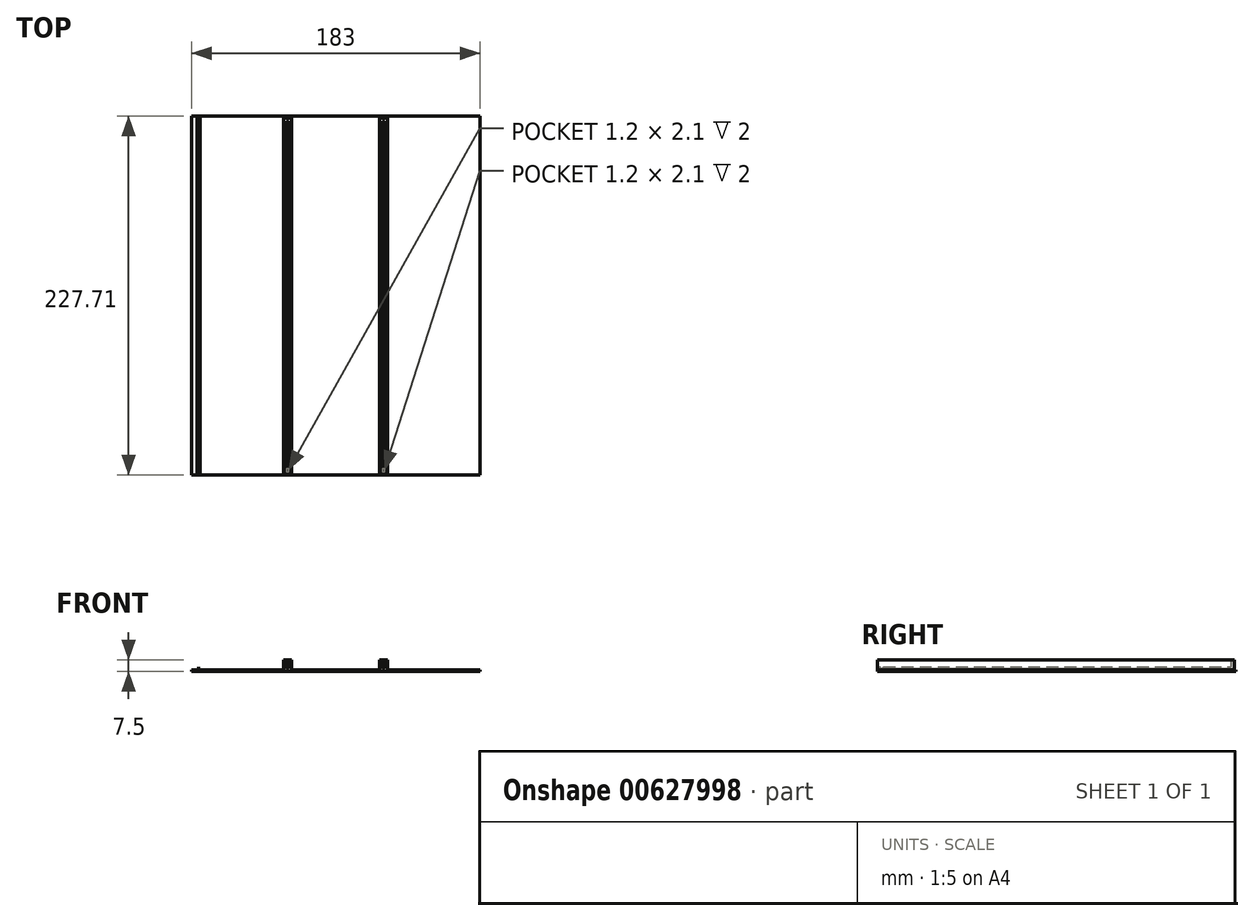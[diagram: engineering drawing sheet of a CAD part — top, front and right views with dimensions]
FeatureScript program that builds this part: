
annotation { "Feature Type Name" : "Feature", "Feature Type Description" : "" }
export const myFeature = defineFeature(function(context is Context, id is Id, definition is map)
    precondition{}
    {
        {
            var Q0;
            Q0=qCreatedBy(makeId("Top.planeOp"),FACE);
            var sketch = newSketch(context, id + "F0", { "sketchPlane" : qUnion([Q0])});
            skLineSegment(sketch, "E0.bottom", {"start": v(0, 0) * mm, "end": v(5.2, 0) * mm});
            skLineSegment(sketch, "E0.top", {"start": v(0, 226.71) * mm, "end": v(5.2, 226.71) * mm});
            skLineSegment(sketch, "E0.left", {"start": v(0, 0) * mm, "end": v(0, 226.71) * mm});
            skLineSegment(sketch, "E0.right", {"start": v(5.2, 0) * mm, "end": v(5.2, 226.71) * mm});
            skLineSegment(sketch, "E1.1.0.0", {"start": v(66.2, 0) * mm, "end": v(66.2, 226.71) * mm});
            skLineSegment(sketch, "E1.1.0.1", {"start": v(61, 0) * mm, "end": v(61, 226.71) * mm});
            skLineSegment(sketch, "E1.1.0.2", {"start": v(61, 226.71) * mm, "end": v(66.2, 226.71) * mm});
            skLineSegment(sketch, "E1.1.0.3", {"start": v(61, 0) * mm, "end": v(66.2, 0) * mm});
            skLineSegment(sketch, "E1.2.0.0", {"start": v(127.2, 0) * mm, "end": v(127.2, 226.71) * mm});
            skLineSegment(sketch, "E1.2.0.1", {"start": v(122, 0) * mm, "end": v(122, 226.71) * mm});
            skLineSegment(sketch, "E1.2.0.2", {"start": v(122, 226.71) * mm, "end": v(127.2, 226.71) * mm});
            skLineSegment(sketch, "E1.2.0.3", {"start": v(122, 0) * mm, "end": v(127.2, 0) * mm});
            skLineSegment(sketch, "E1.direction1", {"start": v(0, 0) * mm, "end": v(61, 0) * mm, "construction": true});
            skSolve(sketch);
        }
        {
            var Q0;
            Q0=makeQuery(id+"F0.imprint","IMPRINT",FACE,{"disambiguationData":[TD([[makeQuery(id+"F0.imprint","IMPRINT",EDGE,{"derivedFrom":sQuery(id+"F0.wireOp",EDGE,"E0.bottom")}),1.0]])]});
            var Q1;
            Q1=makeQuery(id+"F0.imprint","IMPRINT",FACE,{"disambiguationData":[TD([[makeQuery(id+"F0.imprint","IMPRINT",EDGE,{"derivedFrom":sQuery(id+"F0.wireOp",EDGE,"E1.1.0.0")}),1.0]])]});
            extrude(context, id + "F1", {"entities" : qUnion([Q0, Q1]), "depth" : 2 * mm, "offsetDistance" : 25 * mm});
        }
        {
            var Q0;
            Q0=makeQuery(id+"F1.opExtrude","CAP_FACE",FACE,{"disambiguationData":[OSD([sQuery(id+"F0.wireOp",EDGE,"E0.bottom"),sQuery(id+"F0.wireOp",EDGE,"E0.top"),sQuery(id+"F0.wireOp",EDGE,"E0.left"),sQuery(id+"F0.wireOp",EDGE,"E0.right")])],"isStart":false});
            var sketch = newSketch(context, id + "F2", { "sketchPlane" : qUnion([Q0])});
            skLineSegment(sketch, "E2.bottom", {"start": v(0, 0) * mm, "end": v(2, 0) * mm});
            skLineSegment(sketch, "E2.top", {"start": v(0, 226.71) * mm, "end": v(5.2, 226.71) * mm});
            skLineSegment(sketch, "E2.left", {"start": v(0, 0) * mm, "end": v(0, 226.71) * mm});
            skLineSegment(sketch, "E2.right", {"start": v(5.2, 0) * mm, "end": v(5.2, 226.71) * mm});
            skLineSegment(sketch, "E3.top", {"start": v(2, 224.71) * mm, "end": v(3.2, 224.71) * mm});
            skLineSegment(sketch, "E3.left", {"start": v(2, 0) * mm, "end": v(2, 224.71) * mm});
            skLineSegment(sketch, "E3.right", {"start": v(3.2, 0) * mm, "end": v(3.2, 224.71) * mm});
            skLineSegment(sketch, "E4.trimOffspring", {"start": v(3.2, 0) * mm, "end": v(5.2, 0) * mm});
            skLineSegment(sketch, "E5.1.0.0", {"start": v(61, 0) * mm, "end": v(61, 226.71) * mm});
            skLineSegment(sketch, "E5.1.0.1", {"start": v(66.2, 0) * mm, "end": v(66.2, 226.71) * mm});
            skLineSegment(sketch, "E5.1.0.2", {"start": v(63, 0) * mm, "end": v(63, 224.71) * mm});
            skLineSegment(sketch, "E5.1.0.3", {"start": v(64.2, 0) * mm, "end": v(64.2, 224.71) * mm});
            skLineSegment(sketch, "E5.1.0.4", {"start": v(64.2, 0) * mm, "end": v(66.2, 0) * mm});
            skLineSegment(sketch, "E5.1.0.5", {"start": v(61, 226.71) * mm, "end": v(66.2, 226.71) * mm});
            skLineSegment(sketch, "E5.1.0.6", {"start": v(61, 0) * mm, "end": v(63, 0) * mm});
            skLineSegment(sketch, "E5.1.0.7", {"start": v(63, 224.71) * mm, "end": v(64.2, 224.71) * mm});
            skLineSegment(sketch, "E5.2.0.0", {"start": v(122, 0) * mm, "end": v(122, 226.71) * mm});
            skLineSegment(sketch, "E5.2.0.1", {"start": v(127.2, 0) * mm, "end": v(127.2, 226.71) * mm});
            skLineSegment(sketch, "E5.2.0.2", {"start": v(124, 0) * mm, "end": v(124, 224.71) * mm});
            skLineSegment(sketch, "E5.2.0.3", {"start": v(125.2, 0) * mm, "end": v(125.2, 224.71) * mm});
            skLineSegment(sketch, "E5.2.0.4", {"start": v(125.2, 0) * mm, "end": v(127.2, 0) * mm});
            skLineSegment(sketch, "E5.2.0.5", {"start": v(122, 226.71) * mm, "end": v(127.2, 226.71) * mm});
            skLineSegment(sketch, "E5.2.0.6", {"start": v(122, 0) * mm, "end": v(124, 0) * mm});
            skLineSegment(sketch, "E5.2.0.7", {"start": v(124, 224.71) * mm, "end": v(125.2, 224.71) * mm});
            skLineSegment(sketch, "E5.direction1", {"start": v(0, 0) * mm, "end": v(61, 0) * mm, "construction": true});
            skSolve(sketch);
        }
        {
            var Q0;
            Q0=makeQuery(id+"F2.imprint","IMPRINT",FACE,{"disambiguationData":[TD([[makeQuery(id+"F2.imprint","IMPRINT",EDGE,{"derivedFrom":sQuery(id+"F2.wireOp",EDGE,"E2.bottom")}),1.0]])]});
            var Q1;
            Q1=makeQuery(id+"F2.imprint","IMPRINT",FACE,{"disambiguationData":[TD([[makeQuery(id+"F2.imprint","IMPRINT",EDGE,{"derivedFrom":sQuery(id+"F2.wireOp",EDGE,"E5.1.0.0")}),-1.0]])]});
            extrude(context, id + "F3", {"entities" : qUnion([Q0, Q1]), "operationType" : NewBodyOperationType.ADD, "depth" : 4.5 * mm, "offsetDistance" : 25 * mm});
        }
        {
            var Q0;
            Q0=makeQuery(id+"F1.opExtrude","CAP_FACE",FACE,{"disambiguationData":[OSD([sQuery(id+"F0.wireOp",EDGE,"E0.bottom"),sQuery(id+"F0.wireOp",EDGE,"E0.top"),sQuery(id+"F0.wireOp",EDGE,"E0.left"),sQuery(id+"F0.wireOp",EDGE,"E0.right")])],"isStart":false});
            var sketch = newSketch(context, id + "F4", { "sketchPlane" : qUnion([Q0])});
            skLineSegment(sketch, "E6.bottom", {"start": v(2, 1.9) * mm, "end": v(3.2, 1.9) * mm});
            skLineSegment(sketch, "E6.top", {"start": v(2, 4) * mm, "end": v(3.2, 4) * mm});
            skLineSegment(sketch, "E6.left", {"start": v(2, 1.9) * mm, "end": v(2, 4) * mm});
            skLineSegment(sketch, "E6.right", {"start": v(3.2, 1.9) * mm, "end": v(3.2, 4) * mm});
            skLineSegment(sketch, "E7.1.0.0", {"start": v(63, 1.9) * mm, "end": v(64.2, 1.9) * mm});
            skLineSegment(sketch, "E7.1.0.1", {"start": v(63, 1.9) * mm, "end": v(63, 4) * mm});
            skLineSegment(sketch, "E7.1.0.2", {"start": v(63, 4) * mm, "end": v(64.2, 4) * mm});
            skLineSegment(sketch, "E7.1.0.3", {"start": v(64.2, 1.9) * mm, "end": v(64.2, 4) * mm});
            skLineSegment(sketch, "E7.2.0.0", {"start": v(124, 1.9) * mm, "end": v(125.2, 1.9) * mm});
            skLineSegment(sketch, "E7.2.0.1", {"start": v(124, 1.9) * mm, "end": v(124, 4) * mm});
            skLineSegment(sketch, "E7.2.0.2", {"start": v(124, 4) * mm, "end": v(125.2, 4) * mm});
            skLineSegment(sketch, "E7.2.0.3", {"start": v(125.2, 1.9) * mm, "end": v(125.2, 4) * mm});
            skLineSegment(sketch, "E7.direction1", {"start": v(2, 1.9) * mm, "end": v(63, 1.9) * mm, "construction": true});
            skSolve(sketch);
        }
        {
            var Q0;
            Q0=makeQuery(id+"F4.imprint","IMPRINT",FACE,{"disambiguationData":[TD([[makeQuery(id+"F4.imprint","IMPRINT",EDGE,{"derivedFrom":sQuery(id+"F4.wireOp",EDGE,"E6.bottom")}),1.0]])]});
            var Q1;
            Q1=makeQuery(id+"F4.imprint","IMPRINT",FACE,{"disambiguationData":[TD([[makeQuery(id+"F4.imprint","IMPRINT",EDGE,{"derivedFrom":sQuery(id+"F4.wireOp",EDGE,"E7.1.0.0")}),1.0]])]});
            extrude(context, id + "F5", {"entities" : qUnion([Q0, Q1]), "operationType" : NewBodyOperationType.REMOVE, "oppositeDirection" : true, "depth" : 25 * mm, "offsetDistance" : 25 * mm});
        }
        {
            var Q0;
            Q0=qCreatedBy(makeId("Top.planeOp"),FACE);
            var sketch = newSketch(context, id + "F6", { "sketchPlane" : qUnion([Q0])});
            skLineSegment(sketch, "E8.top", {"start": v(-58.3, 227.71) * mm, "end": v(124.7, 227.71) * mm});
            skLineSegment(sketch, "E9", {"start": v(-58.3, 0) * mm, "end": v(124.7, 0) * mm});
            skLineSegment(sketch, "E10", {"start": v(-58.3, 0) * mm, "end": v(-58.3, 227.71) * mm});
            skLineSegment(sketch, "E11.0", {"start": v(0, 0) * mm, "end": v(0, 226.71) * mm, "construction": true});
            skLineSegment(sketch, "E12", {"start": v(124.7, 0) * mm, "end": v(124.7, 227.71) * mm});
            skSolve(sketch);
        }
        {
            var Q0;
            Q0=makeQuery(id+"F6.imprint","IMPRINT",FACE,{"disambiguationData":[TD([[makeQuery(id+"F6.imprint","IMPRINT",EDGE,{"derivedFrom":sQuery(id+"F6.wireOp",EDGE,"E8.top")}),-1.0]])]});
            var Q1;
            Q1=makeQuery(id+"F6.imprint","IMPRINT",FACE,{"disambiguationData":[TD([[makeQuery(id+"F6.imprint","IMPRINT",EDGE,{"derivedFrom":sQuery(id+"F6.wireOp",EDGE,"uZFtzsWq-rkpd-UInv-WifY-KKwyu96MzPo7.bottom")}),1.0]])]});
            extrude(context, id + "F7", {"entities" : qUnion([Q0, Q1]), "operationType" : NewBodyOperationType.ADD, "oppositeDirection" : true, "depth" : 1 * mm, "offsetDistance" : 25 * mm});
        }
        {
            var Q0;
            {var subQ0=sQuery(id+"F6.wireOp",EDGE,"E8.bottom");var subQ1=sQuery(id+"F6.wireOp",EDGE,"E8.top");var subQ2=sQuery(id+"F6.wireOp",EDGE,"E8.left");var subQ3=sQuery(id+"F6.wireOp",EDGE,"E8.right");Q0=makeQuery(id+"F7.boolean.opBoolean","SPLIT",FACE,{"disambiguationData":[TD([makeQuery(id+"F1.opExtrude","SWEPT_FACE",FACE,{"disambiguationData":[OSD([sQuery(id+"F0.wireOp",EDGE,"E0.bottom")])]})])],"derivedFrom":makeQuery(id+"F7.opExtrude","CAP_FACE",FACE,{"disambiguationData":[OSD([subQ0,subQ1,subQ2,subQ3])],"isStart":true})});}
            var sketch = newSketch(context, id + "F8", { "sketchPlane" : qUnion([Q0])});
            skLineSegment(sketch, "E13.bottom", {"start": v(-52.8, 0) * mm, "end": v(-54.8, 0) * mm});
            skLineSegment(sketch, "E13.top", {"start": v(-52.8, 226.71) * mm, "end": v(-54.8, 226.71) * mm});
            skLineSegment(sketch, "E13.left", {"start": v(-52.8, 0) * mm, "end": v(-52.8, 226.71) * mm});
            skLineSegment(sketch, "E13.right", {"start": v(-54.8, 0) * mm, "end": v(-54.8, 226.71) * mm});
            skSolve(sketch);
        }
        {
            var Q0;
            Q0=makeQuery(id+"F8.imprint","IMPRINT",FACE,{"disambiguationData":[TD([[makeQuery(id+"F8.imprint","IMPRINT",EDGE,{"derivedFrom":sQuery(id+"F8.wireOp",EDGE,"E13.bottom")}),1.0]])]});
            extrude(context, id + "F9", {"entities" : qUnion([Q0]), "operationType" : NewBodyOperationType.ADD, "depth" : 1 * mm, "offsetDistance" : 25 * mm});
        }
        {
            var Q0;
            Q0=makeQuery(id+"F1.opExtrude","CAP_EDGE",EDGE,{"disambiguationData":[OSD([sQuery(id+"F0.wireOp",EDGE,"E0.bottom")])],"isStart":false});
            var Q1;
            Q1=makeQuery(id+"F1.opExtrude","CAP_EDGE",EDGE,{"disambiguationData":[OSD([sQuery(id+"F0.wireOp",EDGE,"E1.1.0.3")])],"isStart":false});
            chamfer(context, id + "F10", {"entities" : qUnion([Q0, Q1]), "width" : 1 * mm, "tangentPropagation" : true});
        }
    });
